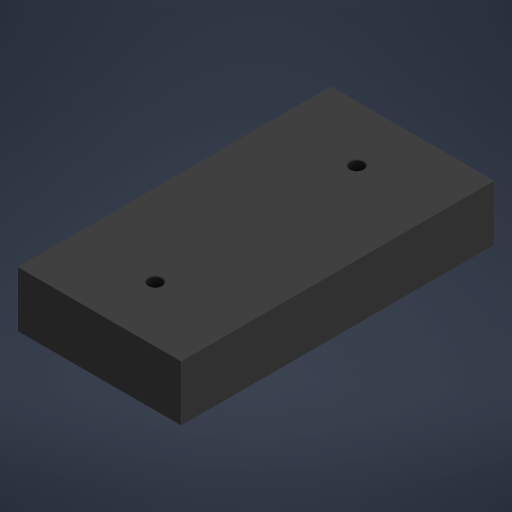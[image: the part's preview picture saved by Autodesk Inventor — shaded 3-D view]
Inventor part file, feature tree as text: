
AUTODESK INVENTOR PART (.ipt)
format: ipt  version: 2023 (Build 270158000, 158)  size: 153,600 bytes
history: native  units: mm
features: extrude x1, other x1
ambient origin geometry x8: Origin, YZ Plane, XZ Plane, XY Plane, X Axis, Y Axis, Z Axis, Center Point
bodies: Solid1 (feature_tree)
feature tree (2):
  extrude  "bat_block"  Depth=47.0mm
  other  "bat_base"
